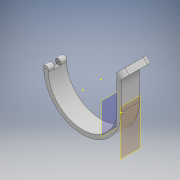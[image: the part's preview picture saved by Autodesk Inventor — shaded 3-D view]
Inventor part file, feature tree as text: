
AUTODESK INVENTOR PART (.ipt)
format: ipt  version: 2018.1 (Build 221171000, 171)  size: 255,488 bytes
history: native  units: mm
features: sketch x24, extrude x10, other x9, split x4, plane x3
ambient origin geometry x8: Origin, YZ Plane, XZ Plane, XY Plane, X Axis, Y Axis, Z Axis, Center Point
bodies: Body1 (feature_tree)
feature tree (50):
  other  "Sólido1"
  extrude  "Extrusión1"  Depth=24.5mm
  extrude  "Extrusión2"  Depth=4.0mm
  sketch  "Boceto3"  dims[d8=0.1mm d9=4.25mm d10=0.0mm]
  other  "Engrosado1"
  extrude  "Extrusión3"  Depth=0.1mm
  sketch  "Boceto4"  dims[d11=0.8mm d12=3.0mm]
  split  "Dividir1"
  other  "Engrosado2"
  extrude  "Extrusión4"  Depth=4.25mm TaperAngle=0.0deg
  sketch  "Boceto6"  dims[d16=4.25mm d17=0.0mm d23=5.0mm]
  extrude  "Extrusión5"  Depth=3.0mm
  sketch  "Boceto8"  dims[d27=26.0mm d28=3.0mm d29=0.0mm]
  sketch  "Boceto9"  dims[d35=5.5mm d36=2.75mm]
  sketch  "Boceto10"  dims[d37=6.5mm]
  plane  "Plano de trabajo1"
  plane  "Plano de trabajo2"
  extrude  "Extrusión8"  Depth=3.0mm TaperAngle=0.0deg
  sketch  "Boceto14"  dims[d39=3.0mm d40=0.0mm]
  extrude  "Extrusión9"  Depth=4.25mm
  extrude  "Extrusión12"  Depth=13.0mm
  sketch  "Boceto23"  dims[d43=3.3mm]
  split  "Dividir3"
  other  "Engrosado3"
  other  "Engrosado4"
  other  "Engrosado5"
  plane  "Plano de trabajo3"
  extrude  "Extrusión13"  Depth=3.0mm TaperAngle=0.0deg
  sketch  "Boceto26"  dims[d46=0.5mm]
  sketch  "Boceto27"  dims[d47=0.5mm]
  sketch  "Boceto28"  dims[d48=0.5mm]
  split  "Dividir4"
  other  "Engrosado6"
  other  "Engrosado7"
  extrude  "Extrusión14"  Depth=5.5mm
  split  "Dividir5"
  other  "Engrosado8"
  sketch  "Boceto 3D1"  dims[d0=27.5mm d1=24.5mm]
  sketch  "Boceto1"  dims[d2=13.0mm d3=0.0mm d4=4.0mm]
  sketch  "Boceto2"  dims[d5=4.35mm d6=0.0mm d7=0.1mm]
  sketch  "Boceto5"  dims[d13=3.0mm d14=6.0mm d15=0.0mm]
  sketch  "Boceto7"  dims[d24=1.6mm d25=0.0mm d26=13.0mm]
  sketch  "Boceto13"  dims[d38=5.5mm]
  sketch  "Boceto15"  dims[d41=2.75mm]
  sketch  "Boceto22"  dims[d42=6.5mm]
  sketch  "Boceto24"  dims[d44=3.0mm]
  sketch  "Boceto25"  dims[d45=3.0mm]
  sketch  "Boceto29"  dims[d49=0.5mm]
  sketch  "Boceto30"  dims[d50=23.0mm]
  sketch  "Boceto31"  dims[d51=3.0mm d52=0.0mm d53=45.0deg d54=13.0mm d55=13.0mm d56=1.0mm d57=1.0mm d58=7.0mm d59=7.0mm d60=7.0mm d61=4.243mm d62=0.0mm d63=4.0mm d64=4.243mm d65=4.243mm]
